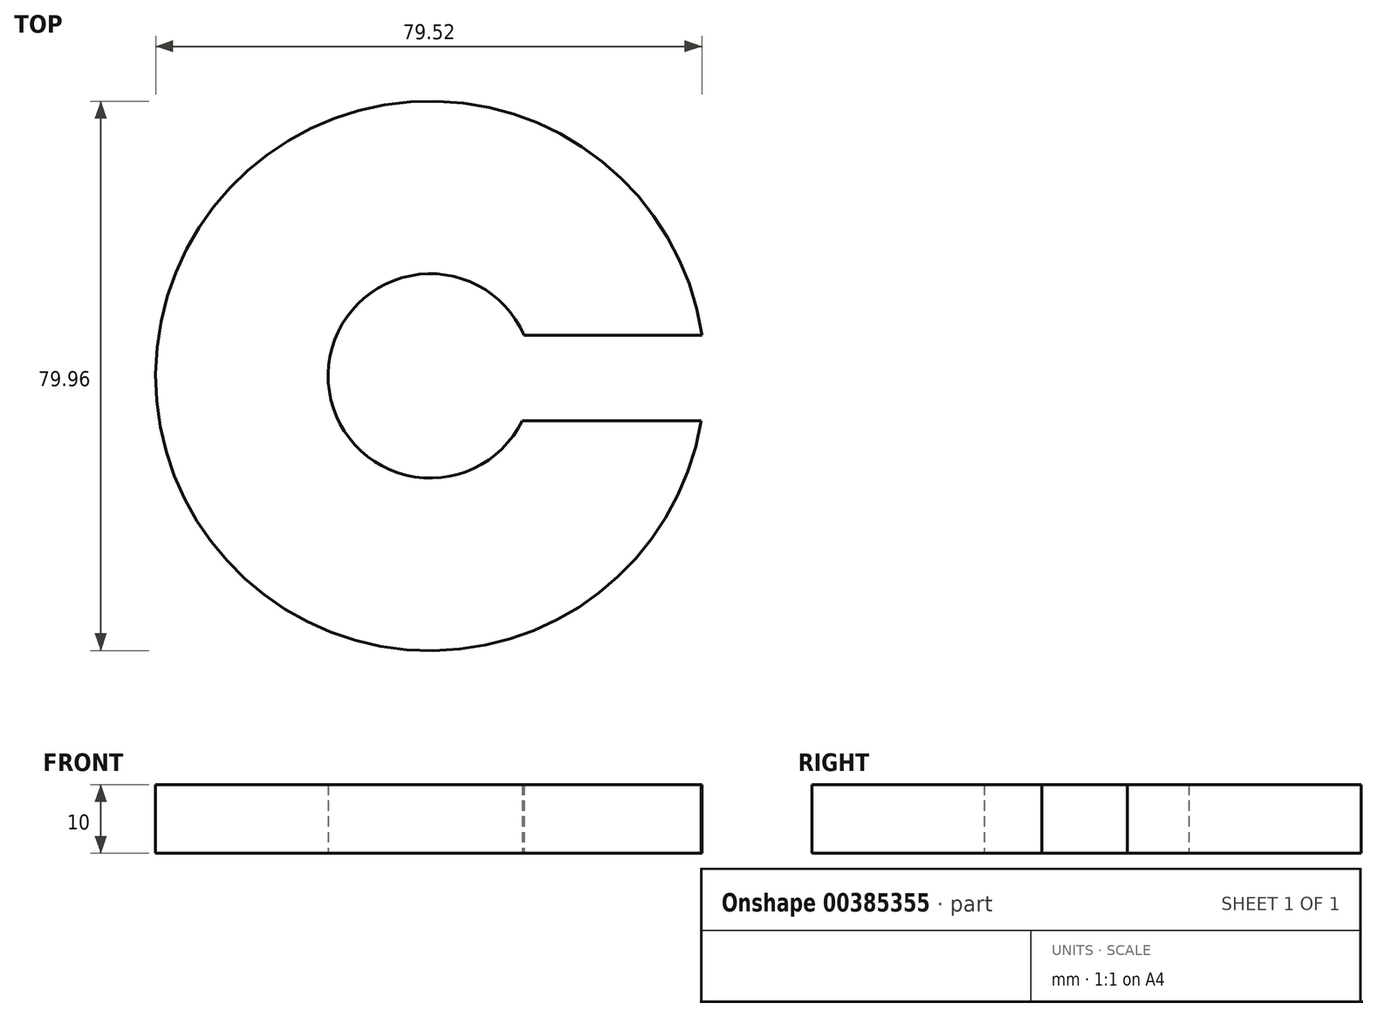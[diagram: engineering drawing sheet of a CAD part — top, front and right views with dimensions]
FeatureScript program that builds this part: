
annotation { "Feature Type Name" : "Feature", "Feature Type Description" : "" }
export const myFeature = defineFeature(function(context is Context, id is Id, definition is map)
    precondition{}
    {
        {
            var Q0;
            Q0=qCreatedBy(makeId("Top.planeOp"),FACE);
            var sketch = newSketch(context, id + "F0", { "sketchPlane" : qUnion([Q0])});
            skArc(sketch, "E0", {"start": v(39.54, 5.95) * mm, "mid": v(-39.98, 0.29) * mm, "end": v(39.45, -6.52) * mm});
            skArc(sketch, "E1", {"start": v(13.63, 5.95) * mm, "mid": v(-14.87, 0.31) * mm, "end": v(13.37, -6.52) * mm});
            skLineSegment(sketch, "E2.bottom", {"start": v(13.63, 5.95) * mm, "end": v(39.54, 5.95) * mm});
            skLineSegment(sketch, "E2.top", {"start": v(13.37, -6.52) * mm, "end": v(39.45, -6.52) * mm});
            skSolve(sketch);
        }
        {
            var Q0;
            Q0 = qSketchRegion(id + "F0", true);
            extrude(context, id + "F1", {"entities" : qUnion([Q0]), "depth" : 10 * mm});
        }
    });
